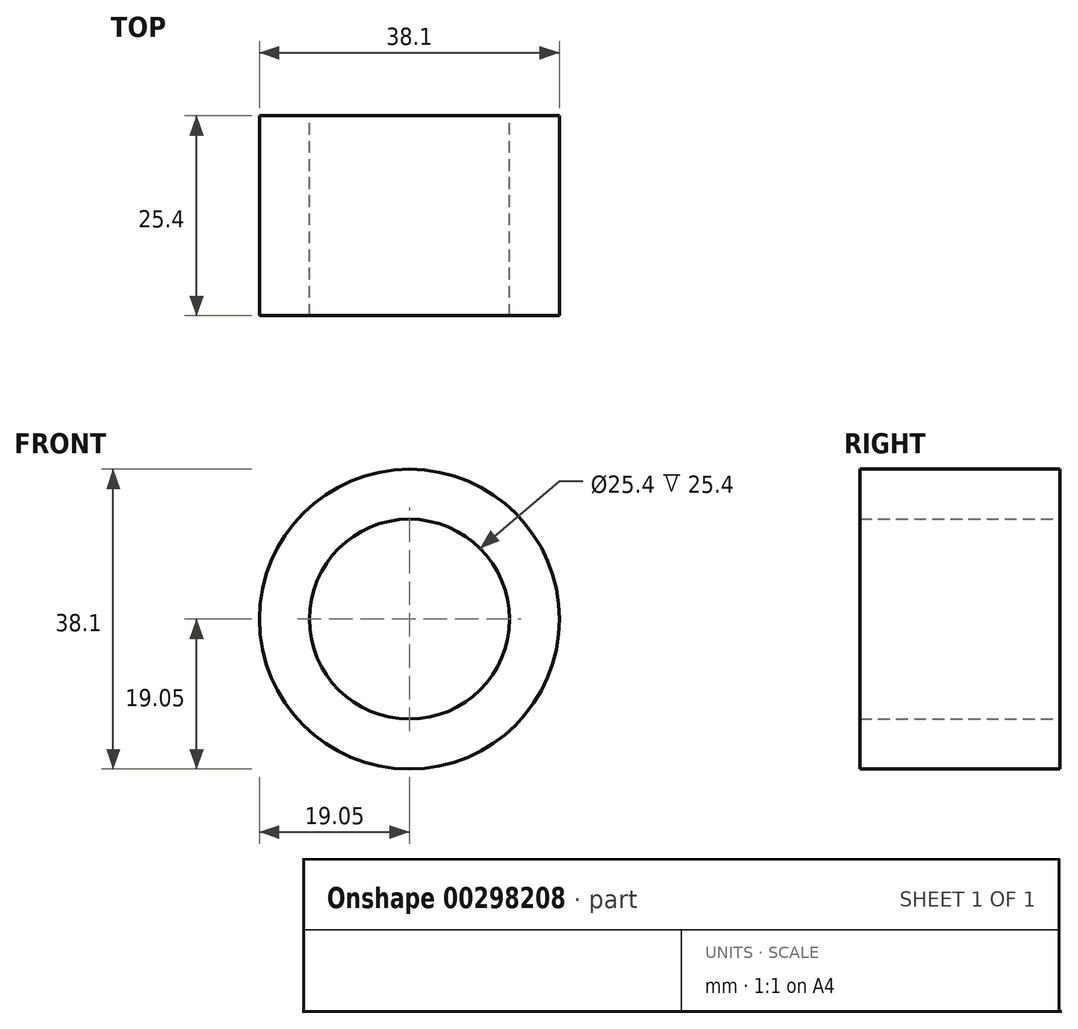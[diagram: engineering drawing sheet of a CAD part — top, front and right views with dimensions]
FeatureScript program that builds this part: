
annotation { "Feature Type Name" : "Feature", "Feature Type Description" : "" }
export const myFeature = defineFeature(function(context is Context, id is Id, definition is map)
    precondition{}
    {
        {
            var Q0;
            Q0=qCreatedBy(makeId("Front.planeOp"),FACE);
            var sketch = newSketch(context, id + "F0", { "sketchPlane" : qUnion([Q0])});
            skCircle(sketch, "E0", {"center": v(0, 0) * mm, "radius": 19.05 * mm});
            skCircle(sketch, "E1.0", {"center": v(0, 0) * mm, "radius": 12.7 * mm});
            skSolve(sketch);
        }
        {
            var Q0;
            Q0 = qSketchRegion(id + "F0", true);
            extrude(context, id + "F1", {"entities" : qUnion([Q0]), "depth" : 25.4 * mm});
        }
    });
